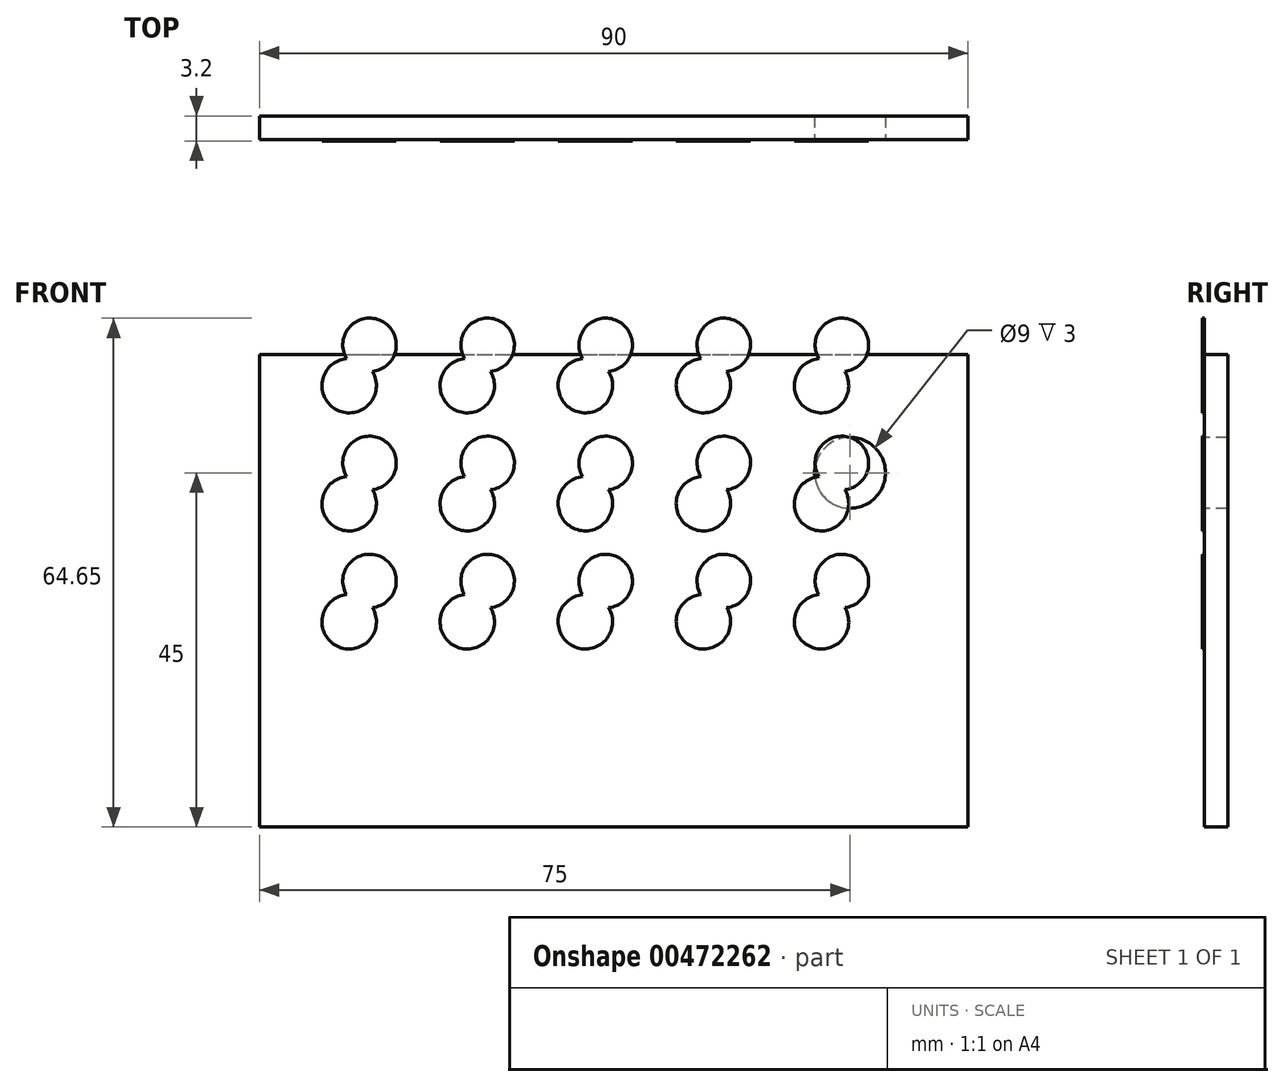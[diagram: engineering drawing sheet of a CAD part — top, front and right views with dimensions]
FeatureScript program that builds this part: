
annotation { "Feature Type Name" : "Feature", "Feature Type Description" : "" }
export const myFeature = defineFeature(function(context is Context, id is Id, definition is map)
    precondition{}
    {
        {
            var Q0;
            Q0=qCreatedBy(makeId("Front.planeOp"),FACE);
            var sketch = newSketch(context, id + "F0", { "sketchPlane" : qUnion([Q0])});
            skLineSegment(sketch, "E0.bottom", {"start": v(0, 0) * mm, "end": v(90, 0) * mm});
            skLineSegment(sketch, "E0.top", {"start": v(0, 60) * mm, "end": v(90, 60) * mm});
            skLineSegment(sketch, "E0.left", {"start": v(0, 0) * mm, "end": v(0, 60) * mm});
            skLineSegment(sketch, "E0.right", {"start": v(90, 0) * mm, "end": v(90, 60) * mm});
            skSolve(sketch);
        }
        {
            var Q0;
            Q0 = qSketchRegion(id + "F0", true);
            extrude(context, id + "F1", {"entities" : qUnion([Q0]), "depth" : 3 * mm});
        }
        {
            var Q0;
            Q0=makeQuery(id+"F1.opExtrude","CAP_FACE",FACE,{"disambiguationData":[OSD([sQuery(id+"F0.wireOp",EDGE,"E0.bottom"),sQuery(id+"F0.wireOp",EDGE,"E0.top"),sQuery(id+"F0.wireOp",EDGE,"E0.left"),sQuery(id+"F0.wireOp",EDGE,"E0.right")])],"isStart":false});
            var sketch = newSketch(context, id + "F2", { "sketchPlane" : qUnion([Q0])});
            skCircle(sketch, "E1", {"center": v(75, 45) * mm, "radius": 4.5 * mm});
            skSolve(sketch);
        }
        {
            var Q0;
            Q0 = qSketchRegion(id + "F2", true);
            extrude(context, id + "F3", {"entities" : qUnion([Q0]), "operationType" : NewBodyOperationType.REMOVE, "oppositeDirection" : true, "depth" : 25 * mm});
        }
        {
            var Q0;
            Q0=makeQuery(id+"F1.opExtrude","CAP_FACE",FACE,{"disambiguationData":[OSD([sQuery(id+"F0.wireOp",EDGE,"E0.bottom"),sQuery(id+"F0.wireOp",EDGE,"E0.top"),sQuery(id+"F0.wireOp",EDGE,"E0.left"),sQuery(id+"F0.wireOp",EDGE,"E0.right")])],"isStart":false});
            var sketch = newSketch(context, id + "F4", { "sketchPlane" : qUnion([Q0])});
            skArc(sketch, "E2", {"start": v(11.04, 29.52) * mm, "mid": v(9.83, 22.99) * mm, "end": v(14.33, 27.87) * mm});
            skArc(sketch, "E3", {"start": v(14.33, 27.87) * mm, "mid": v(15.49, 34.3) * mm, "end": v(11.04, 29.52) * mm});
            skArc(sketch, "E4.0.1.0", {"start": v(14.33, 42.87) * mm, "mid": v(15.49, 49.3) * mm, "end": v(11.04, 44.52) * mm});
            skArc(sketch, "E4.0.1.1", {"start": v(11.04, 44.52) * mm, "mid": v(9.83, 37.99) * mm, "end": v(14.33, 42.87) * mm});
            skArc(sketch, "E4.0.2.0", {"start": v(14.33, 57.87) * mm, "mid": v(15.49, 64.3) * mm, "end": v(11.04, 59.52) * mm});
            skArc(sketch, "E4.0.2.1", {"start": v(11.04, 59.52) * mm, "mid": v(9.83, 52.99) * mm, "end": v(14.33, 57.87) * mm});
            skArc(sketch, "E4.1.0.0", {"start": v(29.33, 27.87) * mm, "mid": v(30.49, 34.3) * mm, "end": v(26.04, 29.52) * mm});
            skArc(sketch, "E4.1.0.1", {"start": v(26.04, 29.52) * mm, "mid": v(24.83, 22.99) * mm, "end": v(29.33, 27.87) * mm});
            skArc(sketch, "E4.1.1.0", {"start": v(29.33, 42.87) * mm, "mid": v(30.49, 49.3) * mm, "end": v(26.04, 44.52) * mm});
            skArc(sketch, "E4.1.1.1", {"start": v(26.04, 44.52) * mm, "mid": v(24.83, 37.99) * mm, "end": v(29.33, 42.87) * mm});
            skArc(sketch, "E4.1.2.0", {"start": v(29.33, 57.87) * mm, "mid": v(30.49, 64.3) * mm, "end": v(26.04, 59.52) * mm});
            skArc(sketch, "E4.1.2.1", {"start": v(26.04, 59.52) * mm, "mid": v(24.83, 52.99) * mm, "end": v(29.33, 57.87) * mm});
            skArc(sketch, "E4.2.0.0", {"start": v(44.33, 27.87) * mm, "mid": v(45.49, 34.3) * mm, "end": v(41.04, 29.52) * mm});
            skArc(sketch, "E4.2.0.1", {"start": v(41.04, 29.52) * mm, "mid": v(39.83, 22.99) * mm, "end": v(44.33, 27.87) * mm});
            skArc(sketch, "E4.2.1.0", {"start": v(44.33, 42.87) * mm, "mid": v(45.49, 49.3) * mm, "end": v(41.04, 44.52) * mm});
            skArc(sketch, "E4.2.1.1", {"start": v(41.04, 44.52) * mm, "mid": v(39.83, 37.99) * mm, "end": v(44.33, 42.87) * mm});
            skArc(sketch, "E4.2.2.0", {"start": v(44.33, 57.87) * mm, "mid": v(45.49, 64.3) * mm, "end": v(41.04, 59.52) * mm});
            skArc(sketch, "E4.2.2.1", {"start": v(41.04, 59.52) * mm, "mid": v(39.83, 52.99) * mm, "end": v(44.33, 57.87) * mm});
            skArc(sketch, "E4.3.0.0", {"start": v(59.33, 27.87) * mm, "mid": v(60.49, 34.3) * mm, "end": v(56.04, 29.52) * mm});
            skArc(sketch, "E4.3.0.1", {"start": v(56.04, 29.52) * mm, "mid": v(54.83, 22.99) * mm, "end": v(59.33, 27.87) * mm});
            skArc(sketch, "E4.3.1.0", {"start": v(59.33, 42.87) * mm, "mid": v(60.49, 49.3) * mm, "end": v(56.04, 44.52) * mm});
            skArc(sketch, "E4.3.1.1", {"start": v(56.04, 44.52) * mm, "mid": v(54.83, 37.99) * mm, "end": v(59.33, 42.87) * mm});
            skArc(sketch, "E4.3.2.0", {"start": v(59.33, 57.87) * mm, "mid": v(60.49, 64.3) * mm, "end": v(56.04, 59.52) * mm});
            skArc(sketch, "E4.3.2.1", {"start": v(56.04, 59.52) * mm, "mid": v(54.83, 52.99) * mm, "end": v(59.33, 57.87) * mm});
            skArc(sketch, "E4.4.0.0", {"start": v(74.33, 27.87) * mm, "mid": v(75.49, 34.3) * mm, "end": v(71.04, 29.52) * mm});
            skArc(sketch, "E4.4.0.1", {"start": v(71.04, 29.52) * mm, "mid": v(69.83, 22.99) * mm, "end": v(74.33, 27.87) * mm});
            skArc(sketch, "E4.4.1.0", {"start": v(74.33, 42.87) * mm, "mid": v(75.49, 49.3) * mm, "end": v(71.04, 44.52) * mm});
            skArc(sketch, "E4.4.1.1", {"start": v(71.04, 44.52) * mm, "mid": v(69.83, 37.99) * mm, "end": v(74.33, 42.87) * mm});
            skArc(sketch, "E4.4.2.0", {"start": v(74.33, 57.87) * mm, "mid": v(75.49, 64.3) * mm, "end": v(71.04, 59.52) * mm});
            skArc(sketch, "E4.4.2.1", {"start": v(71.04, 59.52) * mm, "mid": v(69.83, 52.99) * mm, "end": v(74.33, 57.87) * mm});
            skLineSegment(sketch, "E4.direction1", {"start": v(11.38, 26.08) * mm, "end": v(26.38, 26.08) * mm, "construction": true});
            skLineSegment(sketch, "E4.direction2", {"start": v(11.38, 26.08) * mm, "end": v(11.38, 41.08) * mm, "construction": true});
            skSolve(sketch);
        }
        {
            var Q0;
            Q0 = qSketchRegion(id + "F4", true);
            extrude(context, id + "F5", {"entities" : qUnion([Q0]), "operationType" : NewBodyOperationType.ADD, "depth" : 0.2 * mm});
        }
    });
